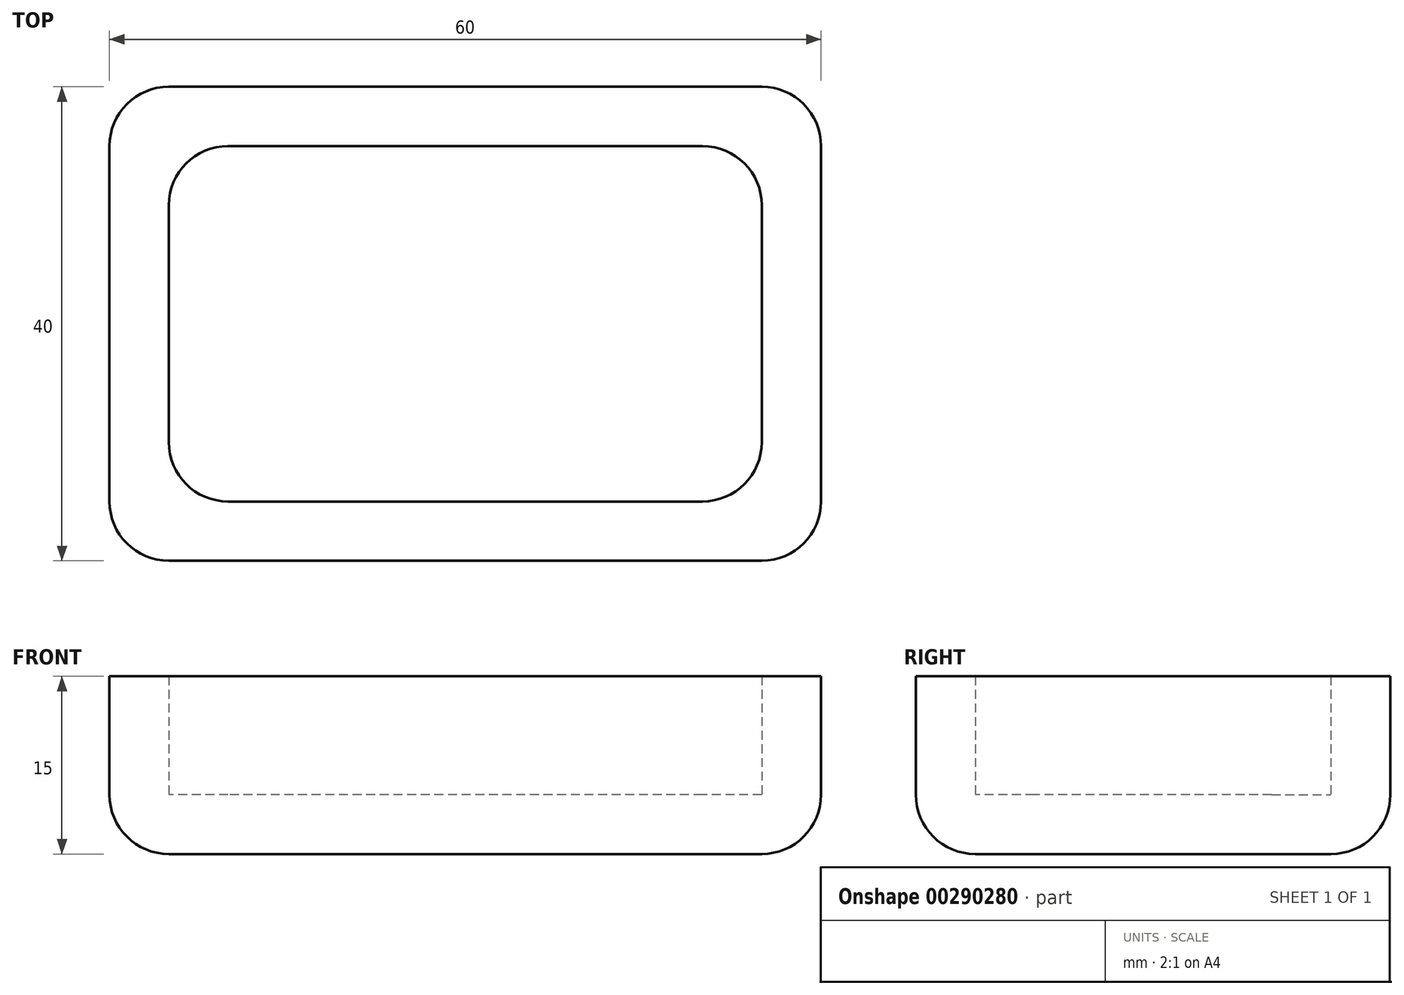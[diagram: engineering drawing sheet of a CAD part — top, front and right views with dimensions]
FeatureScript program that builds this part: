
annotation { "Feature Type Name" : "Feature", "Feature Type Description" : "" }
export const myFeature = defineFeature(function(context is Context, id is Id, definition is map)
    precondition{}
    {
        {
            var Q0;
            Q0=qCreatedBy(makeId("Top.planeOp"),FACE);
            var sketch = newSketch(context, id + "F0", { "sketchPlane" : qUnion([Q0])});
            skLineSegment(sketch, "E0.bottom", {"start": v(30, 20) * mm, "end": v(-30, 20) * mm});
            skLineSegment(sketch, "E0.top", {"start": v(30, -20) * mm, "end": v(-30, -20) * mm});
            skLineSegment(sketch, "E0.left", {"start": v(30, 20) * mm, "end": v(30, -20) * mm});
            skLineSegment(sketch, "E0.right", {"start": v(-30, 20) * mm, "end": v(-30, -20) * mm});
            skPoint(sketch, "E0.middle", {"position": v(0, 0) * mm});
            skSolve(sketch);
        }
        {
            var Q0;
            Q0=qSketchRegion(id+"F0",true);
            extrude(context, id + "F1", {"entities" : qUnion([Q0]), "depth" : 15 * mm});
        }
        {
            var Q0;
            Q0=makeQuery(id+"F1.opExtrude","CAP_FACE",FACE,{"disambiguationData":[OSD([sQuery(id+"F0.wireOp",EDGE,"E0.bottom"),sQuery(id+"F0.wireOp",EDGE,"E0.top"),sQuery(id+"F0.wireOp",EDGE,"E0.left"),sQuery(id+"F0.wireOp",EDGE,"E0.right")])],"isStart":false});
            shell(context, id + "F2", {"entities" : qUnion([Q0]), "thickness" : 5 * mm});
        }
        {
            var Q0;
            Q0=makeQuery(id+"F2.opShell","OFFSET_EDGE",EDGE,{"disambiguationData":[OSD([sQuery(id+"F0.wireOp",EDGE,"E0.bottom"),sQuery(id+"F0.wireOp",EDGE,"E0.right")])]});
            var Q1;
            Q1=makeQuery(id+"F1.opExtrude","SWEPT_EDGE",EDGE,{"disambiguationData":[OSD([sQuery(id+"F0.wireOp",EDGE,"E0.top"),sQuery(id+"F0.wireOp",EDGE,"E0.right")])]});
            var Q2;
            Q2=makeQuery(id+"F1.opExtrude","SWEPT_EDGE",EDGE,{"disambiguationData":[OSD([sQuery(id+"F0.wireOp",EDGE,"E0.top"),sQuery(id+"F0.wireOp",EDGE,"E0.left")])]});
            var Q3;
            Q3=makeQuery(id+"F1.opExtrude","SWEPT_EDGE",EDGE,{"disambiguationData":[OSD([sQuery(id+"F0.wireOp",EDGE,"E0.bottom"),sQuery(id+"F0.wireOp",EDGE,"E0.left")])]});
            var Q4;
            Q4=makeQuery(id+"F1.opExtrude","SWEPT_EDGE",EDGE,{"disambiguationData":[OSD([sQuery(id+"F0.wireOp",EDGE,"E0.bottom"),sQuery(id+"F0.wireOp",EDGE,"E0.right")])]});
            var Q5;
            Q5=makeQuery(id+"F2.opShell","OFFSET_EDGE",EDGE,{"disambiguationData":[OSD([sQuery(id+"F0.wireOp",EDGE,"E0.top"),sQuery(id+"F0.wireOp",EDGE,"E0.right")])]});
            var Q6;
            Q6=makeQuery(id+"F2.opShell","OFFSET_EDGE",EDGE,{"disambiguationData":[OSD([sQuery(id+"F0.wireOp",EDGE,"E0.top"),sQuery(id+"F0.wireOp",EDGE,"E0.left")])]});
            var Q7;
            Q7=makeQuery(id+"F2.opShell","OFFSET_EDGE",EDGE,{"disambiguationData":[OSD([sQuery(id+"F0.wireOp",EDGE,"E0.bottom"),sQuery(id+"F0.wireOp",EDGE,"E0.left")])]});
            var Q8;
            Q8=makeQuery(id+"F1.opExtrude","CAP_EDGE",EDGE,{"disambiguationData":[OSD([sQuery(id+"F0.wireOp",EDGE,"E0.top")])],"isStart":true});
            var Q9;
            Q9=makeQuery(id+"F1.opExtrude","CAP_EDGE",EDGE,{"disambiguationData":[OSD([sQuery(id+"F0.wireOp",EDGE,"E0.left")])],"isStart":true});
            var Q10;
            Q10=makeQuery(id+"F1.opExtrude","CAP_EDGE",EDGE,{"disambiguationData":[OSD([sQuery(id+"F0.wireOp",EDGE,"E0.bottom")])],"isStart":true});
            var Q11;
            Q11=makeQuery(id+"F1.opExtrude","CAP_EDGE",EDGE,{"disambiguationData":[OSD([sQuery(id+"F0.wireOp",EDGE,"E0.right")])],"isStart":true});
            fillet(context, id + "F3", {"entities" : qUnion([Q0, Q1, Q2, Q3, Q4, Q5, Q6, Q7, Q8, Q9, Q10, Q11]), "radius" : 5 * mm, "tangentPropagation" : true, "allowEdgeOverflow" : false});
        }
    });
